# Revit family: Endura
name_source: partatom
category: Lighting Fixtures
units: mm (PartAtom-declared; Revit-internal decimal feet)

## family parameters
Cut with Voids When Loaded = No
Host = Face
Light Source = No
OmniClass Number = 23.80.70.11
OmniClass Title = Luminaries for Internal Lighting
Part Type = Normal
Room Calculation Point = No
Round Connector Dimension = Use Diameter
Shared = No

## types (12) — shared parameters
Apparent Load = 0 VA
Default Elevation = 48"
Description = The Endura LED Parking Garage luminaire offers a precise optical distribution, called ‘’Drive Lane Optics’’, that minimizes glare to the driver while lighting the spaces between the cars.
Glass = White Glass
Lamp = LED Lamp
Manufacturer = Beacon Products
Model = EDR
Nominal Watts = 110 W
URL = https://www.currentlighting.com
Voltage = 120 V

## per-type parameters (varying)
| type | Backbox | Photometric Web |
| EDR-BBT | Black Textured | 2x2 : 24NB-2X2-55W |
| EDR-BMT | Black Matte Textured | 2x2 : 24NB-2X2-55W |
| EDR-WHT | White | 5x5 : 24NB-55W-5X5 |
| EDR-BZT | Bronze Textured | 2x2 : 24NB-2X2-55W |
| EDR-MBT | Mettalic Bronze Textured | 2x2 : 24NB-2X2-55W |
| EDR-DBT | Dark  Bronze Textured | T5W : 60E-AMB-79W-T5 |
| EDR-GYS | Grey smooth | 2x2 : 24NB-2X2-55W |
| EDR-DPS | Dark Platinum Smooth | 2x2 : 24NB-2X2-55W |
| EDR-GNT | Green Textured | T5W : 36E-AMB-48W-T5 |
| EDR-MST | Mettallic Silver Textured | 2x2 : 24NB-2X2-55W |
| EDR-MTT | Metallic titanium textured | 2x2 : 24NB-2X2-55W |
| EDR-OWI | Old World Iron | 2x2 : 24NB-2X2-55W |

## geometry (parser evidence)
native form markers: Blend x56, Sweep x19
no freeform markers — native parametric forms only
